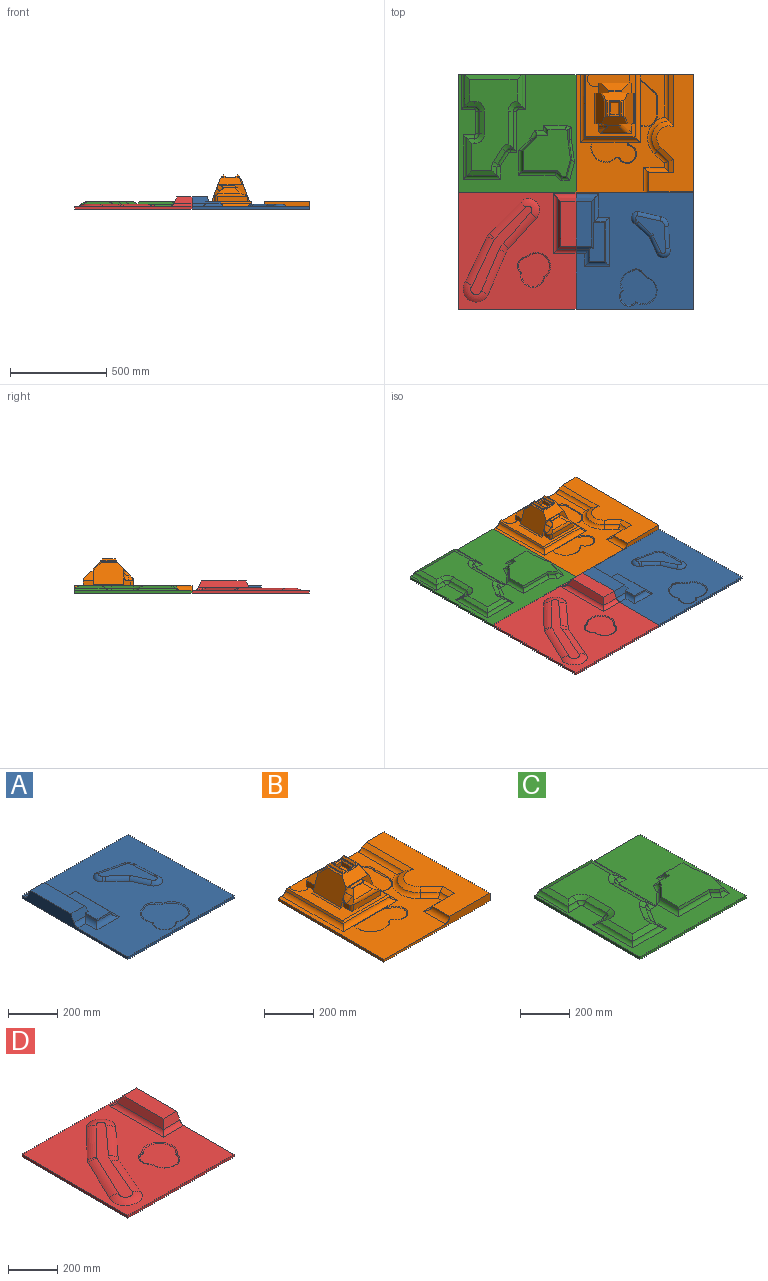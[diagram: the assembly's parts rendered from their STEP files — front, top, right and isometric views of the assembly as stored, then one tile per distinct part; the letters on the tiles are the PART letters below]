
ASSEMBLY  parts=4 mates=4
PART A: 37 faces, bbox 609.6x609.6x63.5 mm
  f0: plane 609.6x609.6mm, normal (0,0,1), area 260229.5mm2, adj f3,f4,f5,f6,f16,f17,f18,f19
  f1: plane 89.79x36.17mm, normal (0,-0.91,0.42), area 3176.7mm2, adj f2,f3,f8,f10,f14,f34,f36
  f2: plane 260.75x36.17mm, normal (0.91,0,0.42), area 8262.5mm2, adj f1,f8,f9,f13,f14,f31,f32
  f3: plane 609.6x63.5mm, normal (-1,0,0), area 20822.2mm2, adj f0,f1,f4,f6,f7,f8,f9,f30
  f4: plane 609.6x12.7mm, normal (0,-1,0), area 7741.9mm2, adj f0,f3,f5,f7
  f5: plane 609.6x12.7mm, normal (1,0,0), area 7741.9mm2, adj f0,f4,f6,f7
  f6: plane 609.6x12.7mm, normal (0,1,0), area 7741.9mm2, adj f0,f3,f5,f7
  f7: plane 609.6x609.6mm, normal (0,0,-1), area 371612.2mm2, adj f3,f4,f5,f6
  f8: plane 232.02x77.91mm, normal (0,0,1), area 18077.3mm2, adj f1,f2,f3,f9
  f9: plane 94.76x36.13mm, normal (0,0.91,0.42), area 3442.2mm2, adj f2,f3,f8,f30
  f10: plane 68.51x6.57mm, normal (-0.97,0,0.26), area 449.8mm2, adj f1,f11,f14,f36
  f11: plane 81.43x6.57mm, normal (0,-0.97,0.26), area 542.2mm2, adj f10,f12,f14,f35
  f12: plane 206.44x6.57mm, normal (0.97,0,0.26), area 1393mm2, adj f11,f13,f14,f33
  f13: plane 61.24x6.57mm, normal (0,0.97,0.26), area 400.4mm2, adj f2,f12,f14,f32
  f14: plane 202.91x77.9mm, normal (0,0,1), area 13298.6mm2, adj f1,f2,f10,f11,f12,f13
  f15: plane 185.84x184.12mm, normal (0,0,1), area 25592mm2, adj f16,f17,f18,f19,f20
  f16: torus R=72.91mm, axis (0,0,1), area 795.5mm2, adj f0,f15,f17,f18
  f17: torus R=36.55mm, axis (0,0,1), area 338.3mm2, adj f0,f15,f16,f19
  f18: torus R=48.7mm, axis (0,0,1), area 914.9mm2, adj f0,f15,f16,f20
  f19: torus R=72.91mm, axis (0,0,1), area 214.2mm2, adj f0,f15,f17,f20
  f20: torus R=73.22mm, axis (0,0,1), area 1459.1mm2, adj f0,f15,f18,f19
  f21: plane 195.07x157.22mm, normal (0,0,1), area 12725.4mm2, adj f22,f23,f24,f25,f26,f27,f28,f29
  f22: torus R=28.17mm, axis (0,0,-1), area 1406.5mm2, adj f0,f21,f23,f24
  f23: cylinder r=25.4mm len=129.85mm, axis (0.98,-0.22,0), area 3352.1mm2, adj f0,f21,f22,f25
  f24: cylinder r=25.4mm len=119.64mm, axis (-0.04,1,0), area 3078.5mm2, adj f0,f21,f22,f26
  f25: torus R=12.61mm, axis (0,0,-1), area 1500mm2, adj f0,f21,f23,f27
  f26: torus R=14.25mm, axis (0,0,-1), area 2249.3mm2, adj f0,f21,f24,f28
  f27: cylinder r=25.4mm len=24.94mm, axis (-0.74,0.68,0), area 327.7mm2, adj f0,f21,f25,f29
  f28: cylinder r=25.4mm len=96.77mm, axis (0.41,-0.91,0), area 2492.6mm2, adj f0,f21,f26,f29
  f29: cylinder r=25.4mm len=90.34mm, axis (0.74,-0.67,0), area 2642.4mm2, adj f0,f21,f27,f28
  f30: cylinder r=25.4mm len=117.78mm, axis (1,0,0), area 3021.4mm2, adj f0,f3,f9,f31
  f31: cylinder r=25.4mm len=144.3mm, axis (0,-1,0), area 3494.6mm2, adj f0,f2,f30,f32
  f32: cylinder r=25.4mm len=82.71mm, axis (1,0,0), area 1920.7mm2, adj f0,f2,f13,f31,f33
  f33: cylinder r=25.4mm len=255.51mm, axis (0,-1,0), area 7538.8mm2, adj f0,f12,f32,f35
  f34: cylinder r=25.4mm len=68.05mm, axis (-1,0,0), area 1670.2mm2, adj f0,f1,f3,f36
  f35: cylinder r=25.4mm len=130.5mm, axis (1,0,0), area 3382.4mm2, adj f0,f11,f33,f36
  f36: cylinder r=25.4mm len=89.98mm, axis (0,1,0), area 2162.4mm2, adj f0,f1,f10,f34,f35
PART B: 110 faces, bbox 619.1x619.1x187.3 mm
  f0: plane 322.95x257.42mm, normal (0,0,1), area 23093.7mm2, adj f1,f3,f6,f7,f22,f23,f24,f25
  f1: plane 609.6x38.1mm, normal (0,1,0), area 17165.9mm2, adj f0,f2,f12,f13,f15,f16,f17,f18
  f2: plane 242.26x125.59mm, normal (0,0,1), area 14180.9mm2, adj f1,f77,f78,f85,f92,f93,f100,f101
  f3: plane 176.72x89.95mm, normal (0,-1,0), area 2235mm2, adj f0,f7,f27,f29,f31,f36,f38,f41
  f4: plane 78.48x56.16mm, normal (0,0,1), area 972.7mm2, adj f49,f54,f69,f70,f71,f72,f73,f74
  f5: plane 82.69x0.77mm, normal (0,0,1), area 63.6mm2, adj f35,f40,f41,f52
  f6: plane 55.36x45.45mm, normal (-1,0,0), area 1009.6mm2, adj f0,f9,f28,f89,f90
  f7: plane 48.84x25.59mm, normal (1,0,0), area 1234.8mm2, adj f0,f3,f24,f31,f86
  f8: plane 58.06x58.06mm, normal (0.71,0,0.71), area 2835.9mm2, adj f11,f22,f25,f26,f33,f44
  f9: plane 39.74x39.74mm, normal (-0.71,0,0.71), area 803.3mm2, adj f6,f34,f87,f88,f89,f90
  f10: plane 71.42x4.88mm, normal (0,0,1), area 211.7mm2, adj f34,f45,f86,f88
  f11: plane 65.64x7.89mm, normal (0,0,1), area 517.8mm2, adj f8,f32,f33,f44
  f12: plane 609.6x460.13mm, normal (0,0,1), area 88258.1mm2, adj f1,f13,f14,f78,f79,f80,f81,f82
  f13: plane 609.6x12.7mm, normal (-1,0,0), area 7741.9mm2, adj f1,f12,f14,f16
  f14: plane 609.6x38.1mm, normal (0,-1,0), area 13778mm2, adj f12,f13,f15,f16,f17,f82
  f15: plane 609.6x38.1mm, normal (1,0,0), area 23225.8mm2, adj f1,f14,f16,f17
  f16: plane 609.6x609.6mm, normal (0,0,-1), area 371612.2mm2, adj f1,f13,f14,f15
  f17: plane 609.6x232.19mm, normal (0,0,1), area 85842.2mm2, adj f1,f14,f15,f18,f19,f20,f21,f81
  f18: plane 276.14x29.82mm, normal (-0.42,0,0.91), area 7154.4mm2, adj f1,f17,f19,f77
  f19: cone r=63.12mm half-angle=65deg, axis (0,0,-1), area 5544.6mm2, adj f17,f18,f21,f78
  f20: plane 70.29x26.18mm, normal (-0.42,0,0.91), area 1764.9mm2, adj f17,f21,f80,f81
  f21: plane 84.4x72.99mm, normal (-0.29,-0.31,0.91), area 2402.3mm2, adj f17,f19,f20,f79
  f22: plane 167.24x41.28mm, normal (0,1,0), area 6710.9mm2, adj f0,f8,f23,f25,f32,f33,f107,f109
  f23: plane 53.24x28.58mm, normal (-1,0,0), area 1401mm2, adj f0,f22,f26,f32,f108,f109
  f24: plane 154.56x27.6mm, normal (0,-1,0), area 4257.6mm2, adj f0,f7,f86,f87,f90
  f25: plane 53.24x25.4mm, normal (1,0,0), area 1352.4mm2, adj f0,f8,f22,f26
  f26: plane 206.29x88.9mm, normal (0,1,0), area 3974.4mm2, adj f0,f8,f23,f25,f27,f29,f32,f35
  f27: plane 159.13x117.69mm, normal (-0.94,0,0.34), area 18369.7mm2, adj f3,f26,f28,f36,f39,f42,f43,f89
  f28: plane 45.85x21.77mm, normal (0,-1,0), area 394.7mm2, adj f0,f6,f27,f39
  f29: plane 158.89x117.45mm, normal (0.94,0,0.34), area 18369.7mm2, adj f3,f26,f35,f38,f40,f41
  f30: plane 82.69x0.77mm, normal (0,0,1), area 63.6mm2, adj f36,f42,f43,f47
  f31: plane 43.39x43.39mm, normal (0.71,0,0.71), area 1331.2mm2, adj f3,f7,f86
  f32: plane 58.06x58.06mm, normal (-0.71,0,0.71), area 2835.9mm2, adj f11,f22,f23,f26,f33,f44
  f33: plane 141.84x38.1mm, normal (0,0.71,0.71), area 5589.6mm2, adj f8,f11,f22,f32
  f34: plane 112.4x34.07mm, normal (0,-0.71,0.71), area 3442.3mm2, adj f9,f10,f86,f87,f88
  f35: plane 125.56x38.1mm, normal (0,0.71,0.71), area 5883mm2, adj f5,f26,f29,f40,f43,f46,f49,f53
  f36: plane 125.56x38.1mm, normal (0,-0.71,0.71), area 5883mm2, adj f3,f27,f30,f41,f42,f48,f49,f51
  f37: plane 264.19x7.26mm, normal (0,-0.71,0.71), area 2675.9mm2, adj f0,f75,f76,f84
  f38: plane 158.89x6.82mm, normal (0.57,0,0.82), area 1322.4mm2, adj f0,f3,f26,f29
  f39: plane 158.89x6.82mm, normal (-0.57,0,0.82), area 1322.4mm2, adj f0,f26,f27,f28
  f40: plane 86.44x6.82mm, normal (0.57,0,0.82), area 691.3mm2, adj f5,f29,f35,f41
  f41: plane 45.88x41.11mm, normal (0.6,-0.45,0.67), area 520.8mm2, adj f3,f5,f29,f36,f40
  f42: plane 86.44x6.82mm, normal (-0.57,0,0.82), area 691.3mm2, adj f27,f30,f36,f43
  f43: plane 45.88x41.11mm, normal (-0.6,0.45,0.67), area 520.8mm2, adj f26,f27,f30,f35,f42
  f44: plane 65.64x7.26mm, normal (0,0.71,0.71), area 599mm2, adj f8,f11,f26,f32
  f45: plane 87.71x7.26mm, normal (0,-0.71,0.71), area 722.4mm2, adj f3,f10,f86,f88
  f46: plane 17.01x5.08mm, normal (0,1,0), area 86.4mm2, adj f35,f47,f49,f66
  f47: plane 82.69x5.08mm, normal (-1,0,0), area 420.1mm2, adj f30,f46,f48,f65
  f48: plane 17.01x5.08mm, normal (0,-1,0), area 86.4mm2, adj f36,f47,f49,f67
  f49: plane 85.67x6.57mm, normal (1,0,0), area 423.2mm2, adj f4,f35,f36,f46,f48,f68,f73,f74
  f50: plane 67.45x1.77mm, normal (0,0,1), area 119.3mm2, adj f65,f66,f67,f68
  f51: plane 18.8x5.08mm, normal (0,-1,0), area 95.5mm2, adj f36,f52,f54,f62
  f52: plane 82.69x5.08mm, normal (1,0,0), area 420.1mm2, adj f5,f51,f53,f61
  f53: plane 18.8x5.08mm, normal (0,1,0), area 95.5mm2, adj f35,f52,f54,f63
  f54: plane 85.67x6.57mm, normal (-1,0,0), area 423.2mm2, adj f4,f35,f36,f51,f53,f64,f73,f74
  f55: plane 67.45x3.56mm, normal (0,0,1), area 240.4mm2, adj f61,f62,f63,f64
  f56: plane 57.99x20.32mm, normal (-1,0,0), area 1178.4mm2, adj f57,f59,f60,f70
  f57: plane 40.24x20.32mm, normal (0,-1,0), area 817.7mm2, adj f56,f58,f60,f69
  f58: plane 57.99x20.32mm, normal (1,0,0), area 1178.4mm2, adj f57,f59,f60,f71
  f59: plane 40.24x20.32mm, normal (0,1,0), area 817.7mm2, adj f56,f58,f60,f72
  f60: plane 57.99x40.24mm, normal (0,0,1), area 2333.7mm2, adj f56,f57,f58,f59
  f61: plane 82.69x7.62mm, normal (0.71,0,0.71), area 809mm2, adj f52,f55,f62,f63
  f62: plane 18.8x7.62mm, normal (0,-0.71,0.71), area 120.5mm2, adj f51,f55,f61,f64
  f63: plane 18.8x7.62mm, normal (0,0.71,0.71), area 120.5mm2, adj f53,f55,f61,f64
  f64: plane 82.69x7.62mm, normal (-0.71,0,0.71), area 809mm2, adj f54,f55,f62,f63
  f65: plane 82.69x7.62mm, normal (-0.71,0,0.71), area 809mm2, adj f47,f50,f66,f67
  f66: plane 17.01x7.62mm, normal (0,0.71,0.71), area 101.2mm2, adj f46,f50,f65,f68
  f67: plane 17.01x7.62mm, normal (0,-0.71,0.71), area 101.2mm2, adj f48,f50,f65,f68
  f68: plane 82.69x7.62mm, normal (0.71,0,0.71), area 809mm2, adj f49,f50,f66,f67
  f69: plane 50.4x5.08mm, normal (0,-0.71,0.71), area 325.6mm2, adj f4,f57,f70,f71
  f70: plane 68.15x5.08mm, normal (-0.71,0,0.71), area 453.1mm2, adj f4,f56,f69,f72
  f71: plane 68.15x5.08mm, normal (0.71,0,0.71), area 453.1mm2, adj f4,f58,f69,f72
  f72: plane 50.4x5.08mm, normal (0,0.71,0.71), area 325.6mm2, adj f4,f59,f70,f71
  f73: plane 56.16x3.59mm, normal (0,0.38,0.92), area 218.4mm2, adj f4,f35,f49,f54
  f74: plane 56.16x3.59mm, normal (0,-0.38,0.92), area 218.4mm2, adj f4,f36,f49,f54
  f75: plane 331.54x10.76mm, normal (-0.91,0,0.42), area 3884.3mm2, adj f0,f1,f37,f83,f84
  f76: plane 331.54x10.76mm, normal (0.91,0,0.42), area 3884.3mm2, adj f0,f1,f37,f84,f85
  f77: cylinder r=25.4mm len=240.99mm, axis (0,-1,0), area 6367.4mm2, adj f1,f2,f18,f78
  f78: torus R=110.99mm, axis (0,0,1), area 6213.6mm2, adj f2,f12,f19,f77,f79,f99
  f79: cylinder r=25.4mm len=74.17mm, axis (0.74,-0.68,0), area 2069.2mm2, adj f12,f21,f78,f80
  f80: cylinder r=25.4mm len=55.42mm, axis (0,-1,0), area 1082.2mm2, adj f12,f20,f79,f81
  f81: cylinder r=25.4mm len=155.99mm, axis (-1,0,0), area 4550.3mm2, adj f12,f17,f20,f80,f82
  f82: cylinder r=25.4mm len=127mm, axis (0,-1,0), area 4560.4mm2, adj f12,f14,f17,f81
  f83: cylinder r=25.4mm len=354.54mm, axis (0,-1,0), area 9884.6mm2, adj f1,f12,f75,f84
  f84: cylinder r=25.4mm len=313.47mm, axis (1,0,0), area 9278.1mm2, adj f12,f37,f75,f76,f83,f85,f95
  f85: cylinder r=25.4mm len=354.54mm, axis (0,-1,0), area 9884.6mm2, adj f1,f2,f12,f76,f84,f91
  f86: cylinder r=25.4mm len=75.24mm, axis (-0.58,0.58,0.58), area 1937.3mm2, adj f3,f7,f10,f24,f31,f34,f45,f87
  f87: cylinder r=25.4mm len=155.47mm, axis (1,0,0), area 2661.2mm2, adj f9,f24,f34,f86,f90
  f88: cylinder r=25.4mm len=38.56mm, axis (0.71,0,0.71), area 939.3mm2, adj f3,f9,f10,f34,f45,f89
  f89: bspline ~50.28x33.63mm, area 998mm2, adj f6,f9,f27,f88
  f90: cylinder r=12.7mm len=33.76mm, axis (0,0,-1), area 594.9mm2, adj f0,f6,f9,f24,f87
  f91: plane 240.96x3.78mm, normal (1,0,0), area 757.5mm2, adj f85,f92,f94,f98,f103
  f92: plane 14.03x11.87mm, normal (-0.64,-0.77,0), area 34.6mm2, adj f2,f91,f93,f103
  f93: plane 35.49x31.76mm, normal (-0.67,-0.75,0), area 43.1mm2, adj f2,f92,f103
  f94: plane 238.64x84.84mm, normal (0,0,1), area 15921mm2, adj f91,f98,f99,f100,f101,f102,f103
  f95: plane 191.6x3.53mm, normal (0,-1,0), area 598.7mm2, adj f84,f97,f104,f105
  f96: cylinder r=68.52mm len=17.87mm, axis (0,0,1), area 38.7mm2, adj f12,f97,f104,f106
  f97: plane 228.6x102.25mm, normal (0,0,1), area 18997.4mm2, adj f95,f96,f104,f105,f106
  f98: torus R=55.54mm, axis (0,0,-1), area 370.3mm2, adj f12,f91,f94,f99
  f99: bspline ~25.5x25.4mm, area 169.9mm2, adj f78,f94,f98,f100
  f100: torus R=55.54mm, axis (0,0,-1), area 202.9mm2, adj f2,f94,f99,f101
  f101: cylinder r=5.08mm len=75.07mm, axis (0,1,0), area 450.1mm2, adj f2,f94,f100,f102
  f102: torus R=38.69mm, axis (0,0,-1), area 336.8mm2, adj f2,f94,f101,f103
  f103: cylinder r=5.08mm len=69.77mm, axis (-0.73,0.68,0), area 450.6mm2, adj f2,f91,f92,f93,f94,f102
  f104: torus R=73.7mm, axis (0,0,-1), area 1234.7mm2, adj f12,f95,f96,f97
  f105: torus R=63.81mm, axis (0,0,-1), area 67.2mm2, adj f12,f95,f97,f106
  f106: torus R=44.56mm, axis (0,0,-1), area 1213.9mm2, adj f12,f96,f97,f105
  f107: plane 44.02x3.18mm, normal (-1,0,0), area 139.8mm2, adj f0,f1,f22,f109
  f108: cylinder r=41.38mm len=63.39mm, axis (0,0,1), area 338.7mm2, adj f0,f1,f23,f109
  f109: plane 216.85x63.39mm, normal (0,0,1), area 10256.7mm2, adj f1,f22,f23,f107,f108
PART C: 71 faces, bbox 610.6x610.6x39.1 mm
  f0: plane 609.6x609.6mm, normal (0,0,1), area 162980.2mm2, adj f1,f2,f3,f4,f39,f40,f41,f42
  f1: plane 609.6x26.26mm, normal (0,1,0), area 11908.6mm2, adj f0,f2,f4,f5,f20,f39,f53
  f2: plane 609.6x12.7mm, normal (-1,0,0), area 7741.9mm2, adj f0,f1,f3,f5
  f3: plane 609.6x12.7mm, normal (0,-1,0), area 7741.9mm2, adj f0,f2,f4,f5
  f4: plane 609.6x12.7mm, normal (1,0,0), area 7741.9mm2, adj f0,f1,f3,f5
  f5: plane 609.6x609.6mm, normal (0,0,-1), area 371612.2mm2, adj f1,f2,f3,f4
  f6: plane 473.8x246.2mm, normal (0,0,1), area 75184.7mm2, adj f7,f8,f9,f10,f11,f12,f13,f14
  f7: plane 40.38x25.4mm, normal (0,0.42,0.91), area 775.7mm2, adj f6,f8,f9,f44
  f8: plane 192.37x25.4mm, normal (-0.42,0,0.91), area 4679.6mm2, adj f6,f7,f10,f45
  f9: cone r=25.4mm half-angle=65deg, axis (0,0,1), area 1677.3mm2, adj f6,f7,f11,f43
  f10: plane 155.65x25.4mm, normal (0,-0.42,0.91), area 3650.3mm2, adj f6,f8,f12,f46
  f11: plane 117.79x25.4mm, normal (-0.42,0,0.91), area 3301.1mm2, adj f6,f9,f13,f42
  f12: plane 46.82x25.4mm, normal (0.42,0,0.91), area 956.2mm2, adj f6,f10,f14,f47
  f13: cone r=25.4mm half-angle=65deg, axis (0,0,1), area 1677.3mm2, adj f6,f11,f15,f41
  f14: cone r=25.4mm half-angle=65deg, axis (0,0,1), area 603.3mm2, adj f6,f12,f16,f48
  f15: plane 51.03x25.4mm, normal (0,-0.42,0.91), area 1074.1mm2, adj f6,f13,f17,f40
  f16: plane 82.37x65.05mm, normal (0.36,-0.23,0.91), area 2281.9mm2, adj f6,f14,f19,f49
  f17: plane 163.63x25.4mm, normal (-0.42,0,0.91), area 3874.1mm2, adj f6,f15,f20,f39
  f18: plane 16.04x16.04mm, normal (0,-0.42,0.91), area 142mm2, adj f19,f21,f51
  f19: cone r=25.4mm half-angle=65deg, axis (0,0,1), area 1028.3mm2, adj f6,f16,f18,f21,f50
  f20: plane 297x25.4mm, normal (0,0.42,0.91), area 7611.8mm2, adj f1,f6,f17,f22
  f21: plane 195.27x26.1mm, normal (0.42,0,0.91), area 5100.3mm2, adj f6,f18,f19,f23,f52
  f22: plane 163.84x25.61mm, normal (0.42,0,0.91), area 3874.6mm2, adj f6,f20,f23,f24,f53
  f23: cone r=25.4mm half-angle=65deg, axis (0,0,1), area 1663.2mm2, adj f6,f21,f22,f24,f54
  f24: plane 20.26x20.26mm, normal (0,-0.42,0.91), area 226.5mm2, adj f22,f23,f55
  f25: plane 67.52x62.46mm, normal (-0.66,0.67,0.34), area 1526.5mm2, adj f26,f38,f61,f66,f67,f68
  f26: plane 107.67x12.03mm, normal (-0.94,0,0.34), area 1338.7mm2, adj f25,f27,f38,f61
  f27: plane 181.23x12.03mm, normal (0,-0.94,0.34), area 2280.4mm2, adj f26,f28,f38,f62
  f28: plane 33.28x30.36mm, normal (-0.67,-0.66,0.34), area 519.8mm2, adj f27,f29,f38,f63
  f29: plane 23.19x12.03mm, normal (0,-0.94,0.34), area 263.5mm2, adj f28,f30,f38,f64
  f30: plane 92.44x27.58mm, normal (0.91,-0.24,0.34), area 1192.8mm2, adj f29,f31,f38,f65
  f31: plane 103.94x21.21mm, normal (0.93,0.13,0.34), area 1840mm2, adj f30,f32,f38,f65,f69
  f32: plane 52.78x17.24mm, normal (0.94,0,0.34), area 895.3mm2, adj f31,f33,f38,f56,f70
  f33: plane 16.5x12.03mm, normal (0.31,0.89,0.34), area 189.2mm2, adj f32,f34,f38,f56
  f34: plane 96.73x12.03mm, normal (0,0.94,0.34), area 1205.5mm2, adj f33,f35,f38,f57
  f35: plane 30.83x12.03mm, normal (-0.94,0,0.34), area 338.7mm2, adj f34,f36,f38,f59
  f36: plane 57.41x12.03mm, normal (0,0.94,0.34), area 690.9mm2, adj f35,f37,f38,f60
  f37: plane 25.43x15.85mm, normal (-0.81,0.48,0.34), area 324.9mm2, adj f36,f38,f58,f68
  f38: plane 246.56x239.63mm, normal (0,0,1), area 44324.6mm2, adj f25,f26,f27,f28,f29,f30,f31,f32
  f39: cylinder r=20.32mm len=182.79mm, axis (0,-1,0), area 4298.6mm2, adj f0,f1,f17,f40
  f40: cylinder r=20.32mm len=70.19mm, axis (1,0,0), area 1480.8mm2, adj f0,f15,f39,f41
  f41: torus R=6.24mm, axis (0,0,-1), area 677.9mm2, adj f0,f13,f40,f42
  f42: cylinder r=20.32mm len=117.79mm, axis (0,-1,0), area 2947.4mm2, adj f0,f11,f41,f43
  f43: torus R=6.24mm, axis (0,0,-1), area 677.9mm2, adj f0,f9,f42,f44
  f44: cylinder r=20.32mm len=59.54mm, axis (-1,0,0), area 1214.4mm2, adj f0,f7,f43,f45
  f45: cylinder r=20.32mm len=230.7mm, axis (0,-1,0), area 5221.8mm2, adj f0,f8,f44,f46
  f46: cylinder r=20.32mm len=193.97mm, axis (1,0,0), area 4302.8mm2, adj f0,f10,f45,f47
  f47: cylinder r=20.32mm len=65.98mm, axis (0,1,0), area 1375.6mm2, adj f0,f12,f46,f48
  f48: torus R=6.24mm, axis (0,0,-1), area 243.9mm2, adj f0,f14,f47,f49
  f49: cylinder r=20.32mm len=79.03mm, axis (0.54,0.84,0), area 2037.4mm2, adj f0,f16,f48,f50
  f50: torus R=6.24mm, axis (0,0,-1), area 434mm2, adj f0,f19,f49,f51
  f51: cylinder r=20.32mm len=35.21mm, axis (1,0,0), area 605.5mm2, adj f0,f18,f50,f52
  f52: cylinder r=20.32mm len=213.74mm, axis (0,1,0), area 5072.8mm2, adj f0,f21,f51,f54
  f53: cylinder r=20.32mm len=182.79mm, axis (0,1,0), area 4298.6mm2, adj f0,f1,f22,f55
  f54: torus R=6.24mm, axis (0,0,-1), area 677.9mm2, adj f0,f23,f52,f55
  f55: cylinder r=20.32mm len=39.42mm, axis (1,0,0), area 711mm2, adj f0,f24,f53,f54
  f56: cylinder r=20.32mm len=32.59mm, axis (0.94,-0.33,0), area 542.6mm2, adj f0,f32,f33,f57,f70
  f57: cylinder r=20.32mm len=119.1mm, axis (-1,0,0), area 2644.4mm2, adj f0,f34,f56,f59
  f58: cylinder r=20.32mm len=58.84mm, axis (-0.51,-0.86,0), area 940.1mm2, adj f0,f37,f60,f67
  f59: cylinder r=20.32mm len=45.55mm, axis (0,-1,0), area 656.7mm2, adj f0,f35,f57,f60
  f60: cylinder r=20.32mm len=63.96mm, axis (-1,0,0), area 1230mm2, adj f0,f36,f58,f59
  f61: cylinder r=20.32mm len=127.25mm, axis (0,1,0), area 2879.2mm2, adj f0,f25,f26,f62,f66
  f62: cylinder r=20.32mm len=198.5mm, axis (-1,0,0), area 4557mm2, adj f0,f27,f61,f63
  f63: cylinder r=20.32mm len=48mm, axis (-0.7,0.71,0), area 1008.1mm2, adj f0,f28,f62,f64
  f64: cylinder r=20.32mm len=45.9mm, axis (-1,0,0), area 830.9mm2, adj f0,f29,f63,f65
  f65: cylinder r=20.32mm len=111.27mm, axis (-0.25,-0.97,0), area 2403.6mm2, adj f0,f30,f31,f64,f69
  f66: cylinder r=12.7mm len=63.83mm, axis (-0.71,-0.7,0), area 1121.2mm2, adj f0,f25,f61,f67
  f67: bspline ~26.47x16.29mm, area 251.9mm2, adj f25,f58,f66,f68
  f68: cylinder r=12.7mm len=12.06mm, axis (0.27,-0.21,0.94), area 39.9mm2, adj f25,f37,f38,f67
  f69: cylinder r=12.7mm len=118.52mm, axis (0.13,-0.99,0), area 1714.8mm2, adj f0,f31,f65,f70
  f70: cylinder r=12.7mm len=65.36mm, axis (0,-1,0), area 905.5mm2, adj f0,f32,f56,f69
PART D: 26 faces, bbox 609.6x609.6x63.5 mm
  f0: plane 609.6x609.6mm, normal (0,0,1), area 236586.2mm2, adj f1,f2,f3,f4,f11,f12,f13,f14
  f1: plane 609.6x12.7mm, normal (-1,0,0), area 7741.9mm2, adj f0,f2,f4,f5
  f2: plane 609.6x12.7mm, normal (0,-1,0), area 7741.9mm2, adj f0,f1,f3,f5
  f3: plane 609.6x63.5mm, normal (1,0,0), area 20822.2mm2, adj f0,f2,f4,f5,f6,f7,f9,f23
  f4: plane 609.6x12.7mm, normal (0,1,0), area 7741.9mm2, adj f0,f1,f3,f5
  f5: plane 609.6x609.6mm, normal (0,0,-1), area 371612.2mm2, adj f1,f2,f3,f4
  f6: plane 232.02x77.91mm, normal (0,0,1), area 18077.3mm2, adj f3,f7,f8,f9
  f7: plane 94.76x36.13mm, normal (0,-0.91,0.42), area 3442.2mm2, adj f3,f6,f8,f24
  f8: plane 265.72x36.13mm, normal (-0.91,0,0.42), area 9922.6mm2, adj f6,f7,f9,f25
  f9: plane 94.76x36.13mm, normal (0,0.91,0.42), area 3442.2mm2, adj f3,f6,f8,f23
  f10: plane 458.95x317.88mm, normal (0,0,1), area 25332.9mm2, adj f11,f12,f13,f14,f15,f16,f17,f18
  f11: cylinder r=67.31mm len=232.53mm, axis (-0.39,-0.92,0), area 9922mm2, adj f0,f10,f12,f13
  f12: torus R=28.31mm, axis (0,0,-1), area 6916.5mm2, adj f0,f10,f11,f14
  f13: torus R=115.55mm, axis (0,0,1), area 1331mm2, adj f0,f10,f11,f15
  f14: cylinder r=67.31mm len=255.11mm, axis (0.43,0.9,0), area 11000.8mm2, adj f0,f10,f12,f16
  f15: cylinder r=67.31mm len=184.23mm, axis (-0.67,-0.74,0), area 8914.2mm2, adj f0,f10,f13,f17
  f16: torus R=11.45mm, axis (0,0,-1), area 435.7mm2, adj f0,f10,f14,f18
  f17: torus R=19.79mm, axis (0,0,-1), area 5378.6mm2, adj f0,f10,f15,f18
  f18: cylinder r=67.31mm len=192.53mm, axis (0.7,0.72,0), area 9688.3mm2, adj f0,f10,f16,f17
  f19: plane 172.38x161.96mm, normal (0,0,1), area 20423.4mm2, adj f20,f21,f22
  f20: torus R=47.98mm, axis (0,0,1), area 688mm2, adj f0,f19,f21,f22
  f21: torus R=71.92mm, axis (0,0,1), area 1397.3mm2, adj f0,f19,f20,f22
  f22: torus R=62.92mm, axis (0,0,1), area 1156.3mm2, adj f0,f19,f20,f21
  f23: cylinder r=25.4mm len=117.78mm, axis (1,0,0), area 3021.4mm2, adj f0,f3,f9,f25
  f24: cylinder r=25.4mm len=117.78mm, axis (-1,0,0), area 3021.4mm2, adj f0,f3,f7,f25
  f25: cylinder r=25.4mm len=311.76mm, axis (0,1,0), area 8238.6mm2, adj f0,f8,f23,f24
PLACE A t=(305.7,-1064.69,550.91)mm
PLACE B t=(305.7,-455.09,550.91)mm
PLACE C t=(-303.9,-455.09,550.91)mm
PLACE D t=(-303.9,-1064.69,550.91)mm
MATE fastened C.f3 <-> D.f4  axis (0,-1,0) through (-303.9,-759.89,557.26)mm
MATE planar C.f0 <-> D.f0  axis (0,0,1) through (-249.73,-465.48,563.61)mm
MATE fastened A.f3 <-> D.f3  axis (-1,0,0) through (0.9,-976.93,576.62)mm
MATE planar B.f2 <-> A.f0  axis (0,0,1) through (420.89,-233.8,563.61)mm
